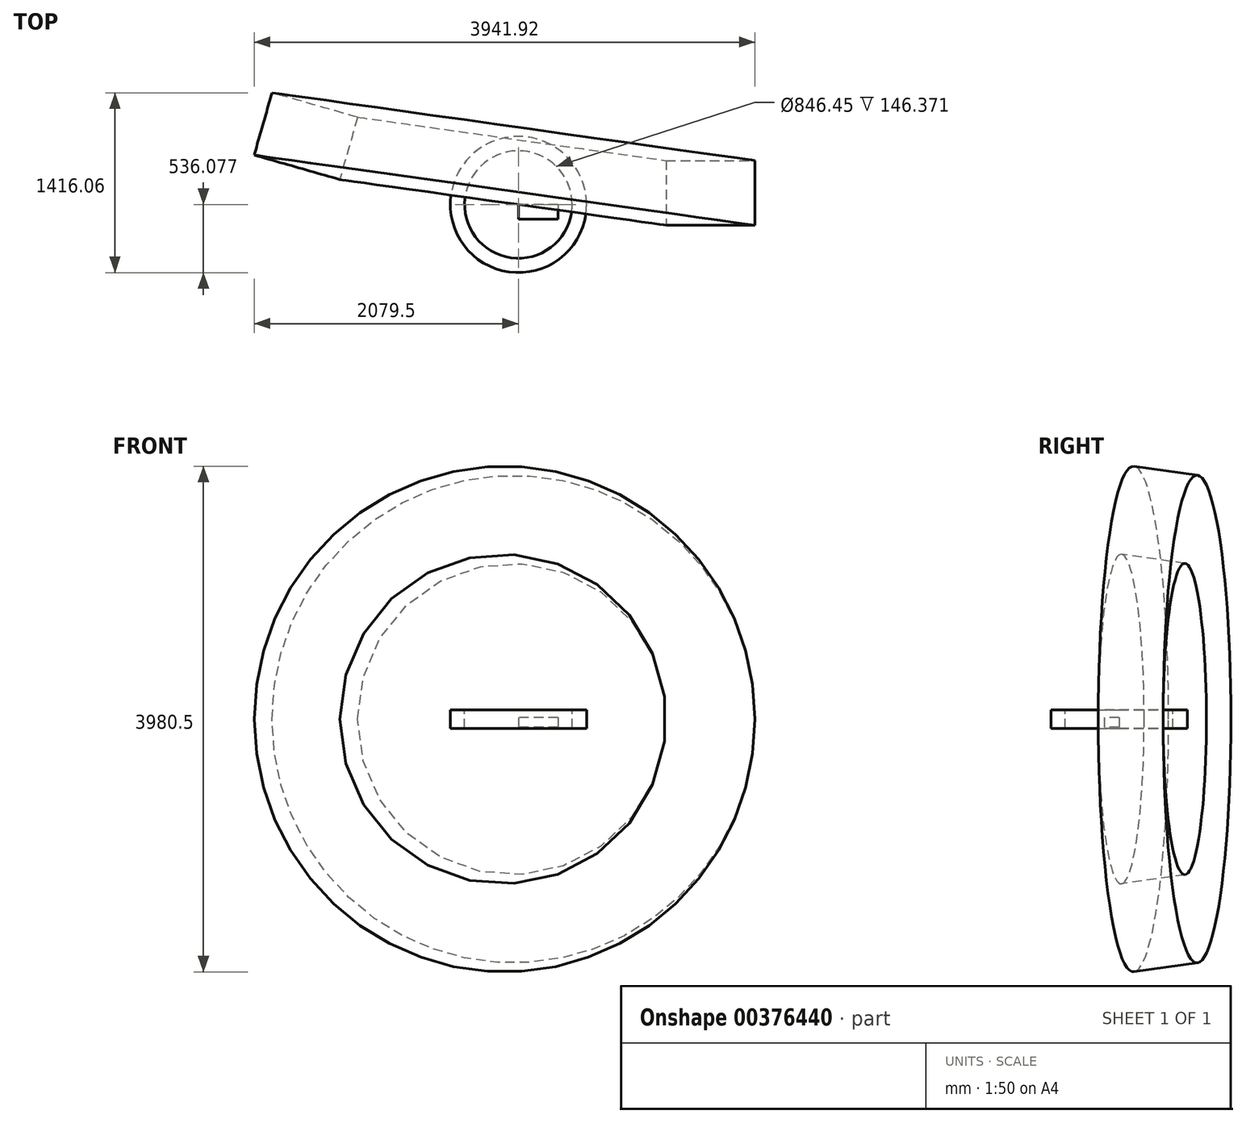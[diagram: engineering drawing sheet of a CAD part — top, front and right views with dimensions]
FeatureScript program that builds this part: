
annotation { "Feature Type Name" : "Feature", "Feature Type Description" : "" }
export const myFeature = defineFeature(function(context is Context, id is Id, definition is map)
    precondition{}
    {
        {
            var Q0;
            Q0=qCreatedBy(makeId("Right.planeOp"),FACE);
            var sketch = newSketch(context, id + "F0", { "sketchPlane" : qUnion([Q0])});
            skLineSegment(sketch, "E0.bottom", {"start": v(214.95, 11.71) * mm, "end": v(98.88, 11.71) * mm});
            skLineSegment(sketch, "E0.top", {"start": v(214.95, -64.8) * mm, "end": v(98.88, -64.8) * mm});
            skLineSegment(sketch, "E0.left", {"start": v(214.95, 11.71) * mm, "end": v(214.95, -64.8) * mm});
            skLineSegment(sketch, "E0.right", {"start": v(98.88, 11.71) * mm, "end": v(98.88, -64.8) * mm});
            skPoint(sketch, "E0.middle", {"position": v(156.91, -26.54) * mm});
            skSolve(sketch);
        }
        {
            var Q0;
            Q0=qCreatedBy(makeId("Front.planeOp"),FACE);
            var sketch = newSketch(context, id + "F1", { "sketchPlane" : qUnion([Q0])});
            skLineSegment(sketch, "E1.0.1", {"start": v(0, -64.8) * mm, "end": v(0, 11.71) * mm});
            skLineSegment(sketch, "E1.0.3", {"start": v(0, 11.71) * mm, "end": v(0, -64.8) * mm});
            skFitSpline(sketch, "E2", {"points": [v(0, -64.8) * mm, v(315.93, -21.94) * mm], "startDerivative": vector(315.93, 42.85) * mm, "endDerivative": vector(273.38, -225.5) * mm});
            skSolve(sketch);
        }
        {
            var Q0;
            Q0=makeQuery(id+"F0.imprint","IMPRINT",FACE,{"disambiguationData":[TD([[makeQuery(id+"F0.imprint","IMPRINT",EDGE,{"derivedFrom":sQuery(id+"F0.wireOp",EDGE,"E0.bottom")}),1.0]])]});
            extrude(context, id + "F2", {"entities" : qUnion([Q0]), "depth" : 311.7 * mm});
        }
        {
            var Q0;
            Q0=qCreatedBy(makeId("Right.planeOp"),FACE);
            var sketch = newSketch(context, id + "F3", { "sketchPlane" : qUnion([Q0])});
            skLineSegment(sketch, "E3.bottom", {"start": v(-321.13, 73.19) * mm, "end": v(-208.28, 73.19) * mm});
            skLineSegment(sketch, "E3.top", {"start": v(-321.13, -73.19) * mm, "end": v(-208.28, -73.19) * mm});
            skLineSegment(sketch, "E3.left", {"start": v(-321.13, 73.19) * mm, "end": v(-321.13, -73.19) * mm});
            skLineSegment(sketch, "E3.right", {"start": v(-208.28, 73.19) * mm, "end": v(-208.28, -73.19) * mm});
            skPoint(sketch, "E3.middle", {"position": v(-264.7, 0) * mm});
            skSolve(sketch);
        }
        {
            var Q0;
            Q0=makeQuery(id+"F3.imprint","IMPRINT",FACE,{"disambiguationData":[TD([[makeQuery(id+"F3.imprint","IMPRINT",EDGE,{"derivedFrom":sQuery(id+"F3.wireOp",EDGE,"E3.bottom")}),-1.0]])]});
            var Q1;
            Q1=makeQuery(id+"F2.opExtrude","CAP_EDGE",EDGE,{"disambiguationData":[OSD([sQuery(id+"F0.wireOp",EDGE,"E0.left")])],"isStart":true});
            revolve(context, id + "F4", {"entities" : qUnion([Q0]), "axis" : qUnion([Q1]), "revolveType" : RevolveType.FULL});
        }
        {
            var Q0;
            Q0=qCreatedBy(makeId("Top.planeOp"),FACE);
            var sketch = newSketch(context, id + "F5", { "sketchPlane" : qUnion([Q0])});
            skLineSegment(sketch, "E4.bottom", {"start": v(1162.23, 51.59) * mm, "end": v(1862.42, 51.59) * mm});
            skLineSegment(sketch, "E4.top", {"start": v(1162.23, 561.72) * mm, "end": v(1862.42, 561.72) * mm});
            skLineSegment(sketch, "E4.left", {"start": v(1162.23, 51.59) * mm, "end": v(1162.23, 561.72) * mm});
            skLineSegment(sketch, "E4.right", {"start": v(1862.42, 51.59) * mm, "end": v(1862.42, 561.72) * mm});
            skLineSegment(sketch, "E5", {"start": v(0, 1101.87) * mm, "end": v(-249.72, -678.57) * mm});
            skSolve(sketch);
        }
        {
            var Q0;
            Q0 = qSketchRegion(id + "F5", true);
            var Q1;
            Q1=sQuery(id+"F5.wireOp",EDGE,"E5");
            revolve(context, id + "F6", {"entities" : qUnion([Q0]), "axis" : qUnion([Q1]), "revolveType" : RevolveType.FULL});
        }
    });
